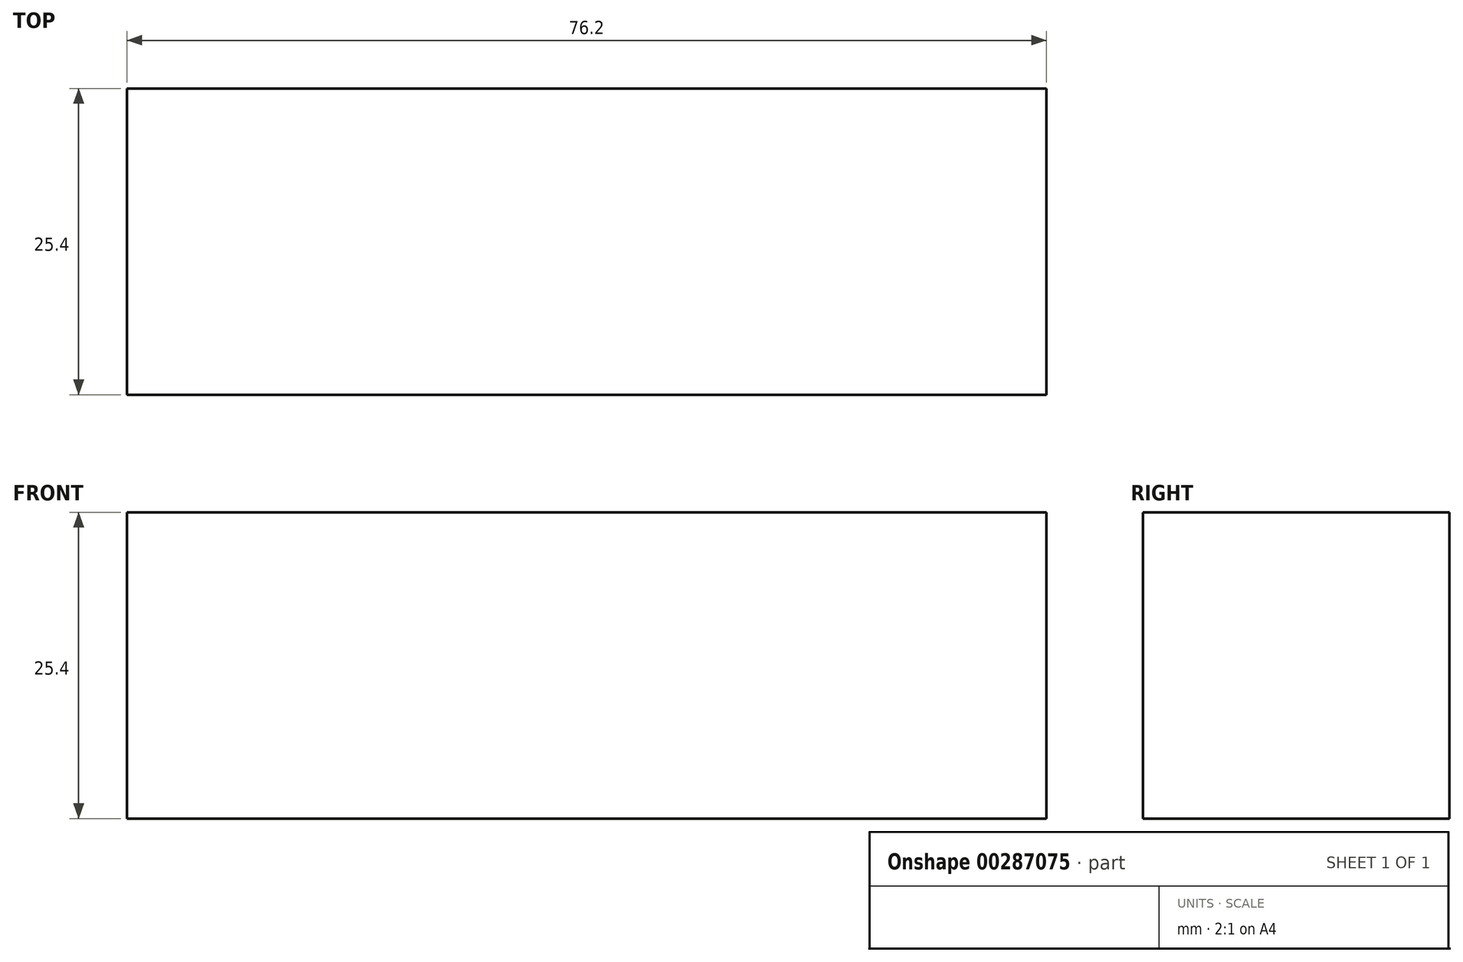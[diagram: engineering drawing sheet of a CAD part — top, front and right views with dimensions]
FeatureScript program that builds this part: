
annotation { "Feature Type Name" : "Feature", "Feature Type Description" : "" }
export const myFeature = defineFeature(function(context is Context, id is Id, definition is map)
    precondition{}
    {
        {
            var Q0;
            Q0=qCreatedBy(makeId("Front.planeOp"),FACE);
            var sketch = newSketch(context, id + "F0", { "sketchPlane" : qUnion([Q0])});
            skLineSegment(sketch, "E0", {"start": v(0, 0) * mm, "end": v(-76.2, 0) * mm});
            skLineSegment(sketch, "E1", {"start": v(-76.2, 0) * mm, "end": v(-76.2, 25.4) * mm});
            skLineSegment(sketch, "E2", {"start": v(-76.2, 25.4) * mm, "end": v(0, 25.4) * mm});
            skLineSegment(sketch, "E3", {"start": v(0, 25.4) * mm, "end": v(0, 0) * mm});
            skSolve(sketch);
        }
        {
            var Q0;
            Q0 = qSketchRegion(id + "F0", true);
            extrude(context, id + "F1", {"entities" : qUnion([Q0]), "depth" : 25.4 * mm});
        }
    });
